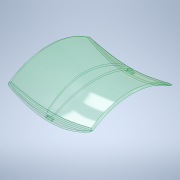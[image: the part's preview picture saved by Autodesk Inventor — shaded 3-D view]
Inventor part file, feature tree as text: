
AUTODESK INVENTOR PART (.ipt)
format: ipt  version: 2020.3 (Build 243373000, 373)  size: 506,880 bytes
history: native  units: mm
features: sketch x4, chamfer x3, extrude x2, fillet x2, projected_geometry x2, sweep x1, plane x1, mirror x1
ambient origin geometry x8: Origin, YZ Plane, XZ Plane, XY Plane, X Axis, Y Axis, Z Axis, Center Point
bodies: Body1 (feature_tree)
feature tree (16):
  sweep  "Sweep1"
  extrude  "Extrusion4"  Depth=4.0mm TaperAngle=45.0deg
  chamfer  "Chamfer1"  Distance=142.009mm
  plane  "Work Plane8"
  mirror  "Mirror2"
  extrude  "Extrusion5"  Depth=3.0mm
  fillet  "Fillet3"  Radius=1.0mm
  chamfer  "Chamfer2"  Distance=1.0mm Angle=45.0deg
  chamfer  "Chamfer3"  Distance=200.0mm
  fillet  "Fillet4"  [1 undecoded]
  sketch  "Sketch2"  dims[d16=0.0mm d17=0.0mm d18=10.0mm]
  sketch  "Sketch6"  dims[d19=4.0mm d20=0.0mm d21=4.0mm d22=2.0mm d23=45.0deg]
  sketch  "Sketch7"  dims[d24=5.0mm]
  projected_geometry  "Projected Loop1"
  sketch  "Sketch8"  dims[d25=2.0mm d26=142.009mm d27=0.0mm d28=3.0mm d29=1.0mm d30=2.0mm d31=45.0deg d32=1.0mm d33=2.0mm d34=45.0deg d35=200.0mm]
  projected_geometry  "Projected Loop2"
note: 1 required parameter value undecoded (feature->parameter linkage not recoverable at this tier; creation-order binding heuristic only, values carry confidence <= 0.55)
